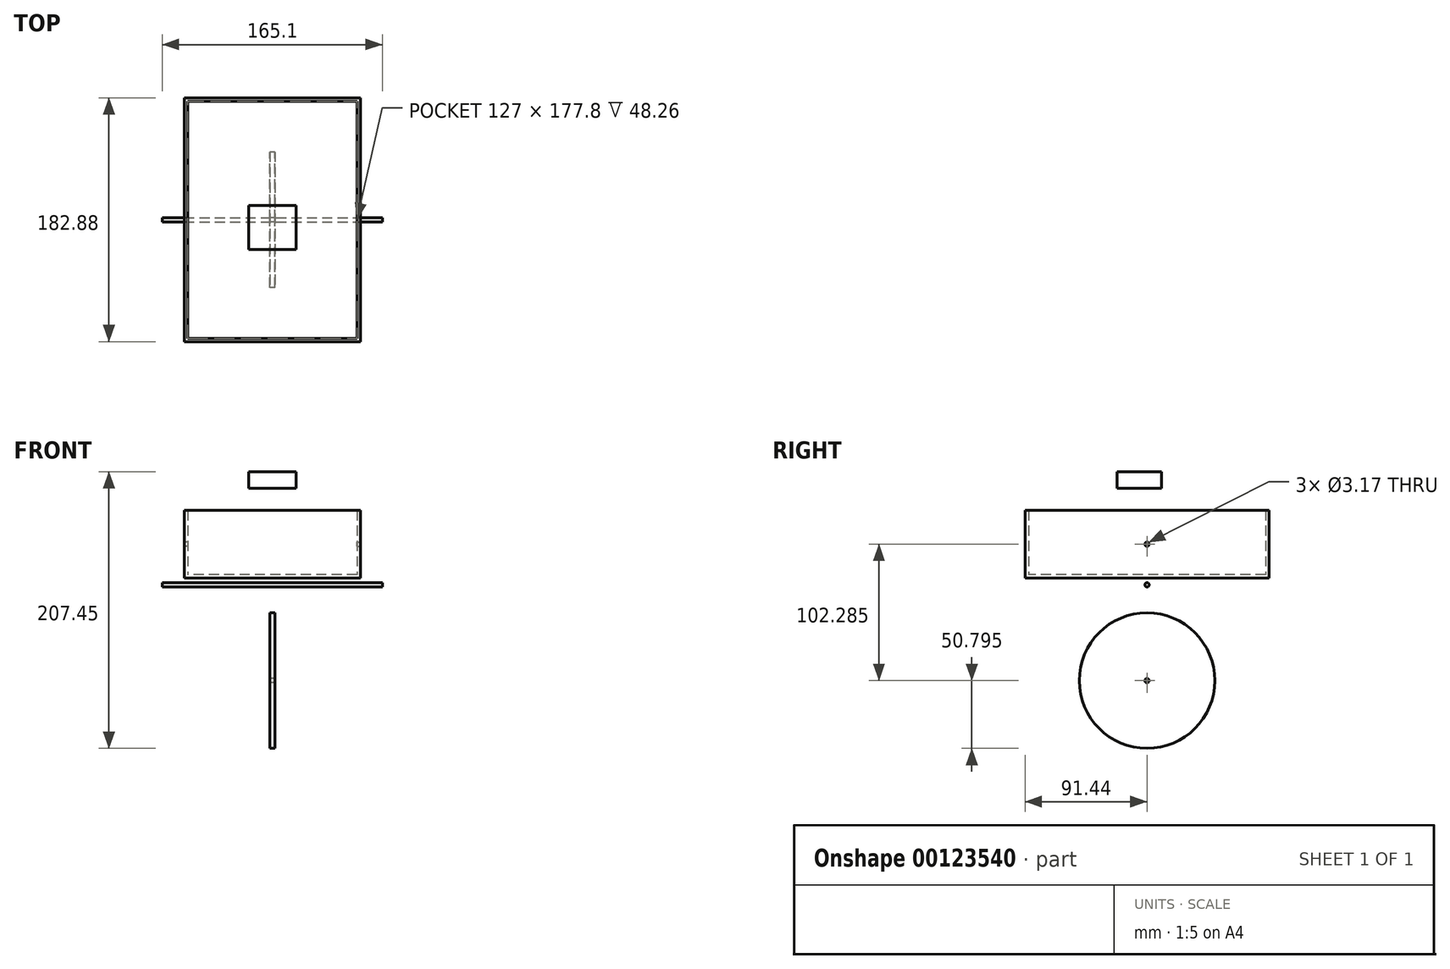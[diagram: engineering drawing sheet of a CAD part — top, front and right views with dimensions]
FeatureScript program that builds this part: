
annotation { "Feature Type Name" : "Feature", "Feature Type Description" : "" }
export const myFeature = defineFeature(function(context is Context, id is Id, definition is map)
    precondition{}
    {
        {
            var Q0;
            Q0=qCreatedBy(makeId("Top.planeOp"),FACE);
            var sketch = newSketch(context, id + "F0", { "sketchPlane" : qUnion([Q0])});
            skLineSegment(sketch, "E0.bottom", {"start": v(63.5, 88.9) * mm, "end": v(-63.5, 88.9) * mm});
            skLineSegment(sketch, "E0.top", {"start": v(63.5, -88.9) * mm, "end": v(-63.5, -88.9) * mm});
            skLineSegment(sketch, "E0.left", {"start": v(63.5, 88.9) * mm, "end": v(63.5, -88.9) * mm});
            skLineSegment(sketch, "E0.right", {"start": v(-63.5, 88.9) * mm, "end": v(-63.5, -88.9) * mm});
            skPoint(sketch, "E0.middle", {"position": v(0, 0) * mm});
            skLineSegment(sketch, "E1.0", {"start": v(66.04, 91.44) * mm, "end": v(-66.04, 91.44) * mm});
            skLineSegment(sketch, "E1.1", {"start": v(66.04, 91.44) * mm, "end": v(66.04, -91.44) * mm});
            skLineSegment(sketch, "E1.2", {"start": v(66.04, -91.44) * mm, "end": v(-66.04, -91.44) * mm});
            skLineSegment(sketch, "E1.3", {"start": v(-66.04, 91.44) * mm, "end": v(-66.04, -91.44) * mm});
            skSolve(sketch);
        }
        {
            var Q0;
            Q0=makeQuery(id+"F0.imprint","IMPRINT",FACE,{"disambiguationData":[TD([[makeQuery(id+"F0.imprint","IMPRINT",EDGE,{"derivedFrom":sQuery(id+"F0.wireOp",EDGE,"E0.bottom")}),1.0]])]});
            extrude(context, id + "F1", {"entities" : qUnion([Q0]), "depth" : 2.54 * mm});
        }
        {
            var Q0;
            Q0=makeQuery(id+"F0.imprint","IMPRINT",FACE,{"disambiguationData":[TD([[makeQuery(id+"F0.imprint","IMPRINT",EDGE,{"derivedFrom":sQuery(id+"F0.wireOp",EDGE,"E0.bottom")}),-1.0]])]});
            extrude(context, id + "F2", {"entities" : qUnion([Q0]), "operationType" : NewBodyOperationType.ADD, "depth" : 50.8 * mm});
        }
        {
            var Q0;
            Q0=makeQuery(id+"F2.opExtrude","SWEPT_FACE",FACE,{"disambiguationData":[OSD([sQuery(id+"F0.wireOp",EDGE,"E1.1")])]});
            var sketch = newSketch(context, id + "F3", { "sketchPlane" : qUnion([Q0])});
            skCircle(sketch, "E2", {"center": v(0, 25.4) * mm, "radius": 1.59 * mm});
            skSolve(sketch);
        }
        {
            var Q0;
            Q0=makeQuery(id+"F3.imprint","IMPRINT",FACE,{"disambiguationData":[TD([[makeQuery(id+"F3.imprint","IMPRINT",EDGE,{"derivedFrom":sQuery(id+"F3.wireOp",EDGE,"E2")}),1.0]])]});
            extrude(context, id + "F4", {"entities" : qUnion([Q0]), "operationType" : NewBodyOperationType.REMOVE, "oppositeDirection" : true, "depth" : 2.54 * mm});
        }
        {
            var Q0;
            Q0=makeQuery(id+"F2.opExtrude","SWEPT_FACE",FACE,{"disambiguationData":[OSD([sQuery(id+"F0.wireOp",EDGE,"E1.3")])]});
            var sketch = newSketch(context, id + "F5", { "sketchPlane" : qUnion([Q0])});
            skCircle(sketch, "E3", {"center": v(0, 25.4) * mm, "radius": 1.59 * mm});
            skSolve(sketch);
        }
        {
            var Q0;
            Q0=makeQuery(id+"F5.imprint","IMPRINT",FACE,{"disambiguationData":[TD([[makeQuery(id+"F5.imprint","IMPRINT",EDGE,{"derivedFrom":sQuery(id+"F5.wireOp",EDGE,"E3")}),1.0]])]});
            extrude(context, id + "F6", {"entities" : qUnion([Q0]), "operationType" : NewBodyOperationType.REMOVE, "oppositeDirection" : true, "depth" : 2.54 * mm});
        }
        {
            var Q0;
            Q0=qCreatedBy(makeId("Right.planeOp"),FACE);
            var sketch = newSketch(context, id + "F7", { "sketchPlane" : qUnion([Q0])});
            skCircle(sketch, "E4", {"center": v(0, -5.08) * mm, "radius": 1.59 * mm});
            skSolve(sketch);
        }
        {
            var Q0;
            Q0 = qSketchRegion(id + "F7", true);
            extrude(context, id + "F8", {"entities" : qUnion([Q0]), "endBound" : BoundingType.SYMMETRIC, "oppositeDirection" : true, "depth" : 165.1 * mm});
        }
        {
            var Q0;
            Q0=qCreatedBy(makeId("Right.planeOp"),FACE);
            var sketch = newSketch(context, id + "F9", { "sketchPlane" : qUnion([Q0])});
            skCircle(sketch, "E5", {"center": v(0, -76.88) * mm, "radius": 50.8 * mm});
            skCircle(sketch, "E6", {"center": v(0, -76.88) * mm, "radius": 1.59 * mm});
            skSolve(sketch);
        }
        {
            var Q0;
            Q0 = qSketchRegion(id + "F9", true);
            extrude(context, id + "F10", {"entities" : qUnion([Q0]), "endBound" : BoundingType.SYMMETRIC, "depth" : 3.8 * mm});
        }
        {
            var Q0;
            Q0=qCreatedBy(makeId("Right.planeOp"),FACE);
            var sketch = newSketch(context, id + "F11", { "sketchPlane" : qUnion([Q0])});
            skLineSegment(sketch, "E7.bottom", {"start": v(-22.4, 79.77) * mm, "end": v(10.79, 79.77) * mm});
            skLineSegment(sketch, "E7.top", {"start": v(-22.4, 67.32) * mm, "end": v(10.79, 67.32) * mm});
            skLineSegment(sketch, "E7.left", {"start": v(-22.4, 79.77) * mm, "end": v(-22.4, 67.32) * mm});
            skLineSegment(sketch, "E7.right", {"start": v(10.79, 79.77) * mm, "end": v(10.79, 67.32) * mm});
            skSolve(sketch);
        }
        {
            var Q0;
            Q0=makeQuery(id+"F11.imprint","IMPRINT",FACE,{"disambiguationData":[TD([[makeQuery(id+"F11.imprint","IMPRINT",EDGE,{"derivedFrom":sQuery(id+"F11.wireOp",EDGE,"E7.bottom")}),-1.0]])]});
            extrude(context, id + "F12", {"entities" : qUnion([Q0]), "endBound" : BoundingType.SYMMETRIC, "depth" : 35.56 * mm});
        }
    });
